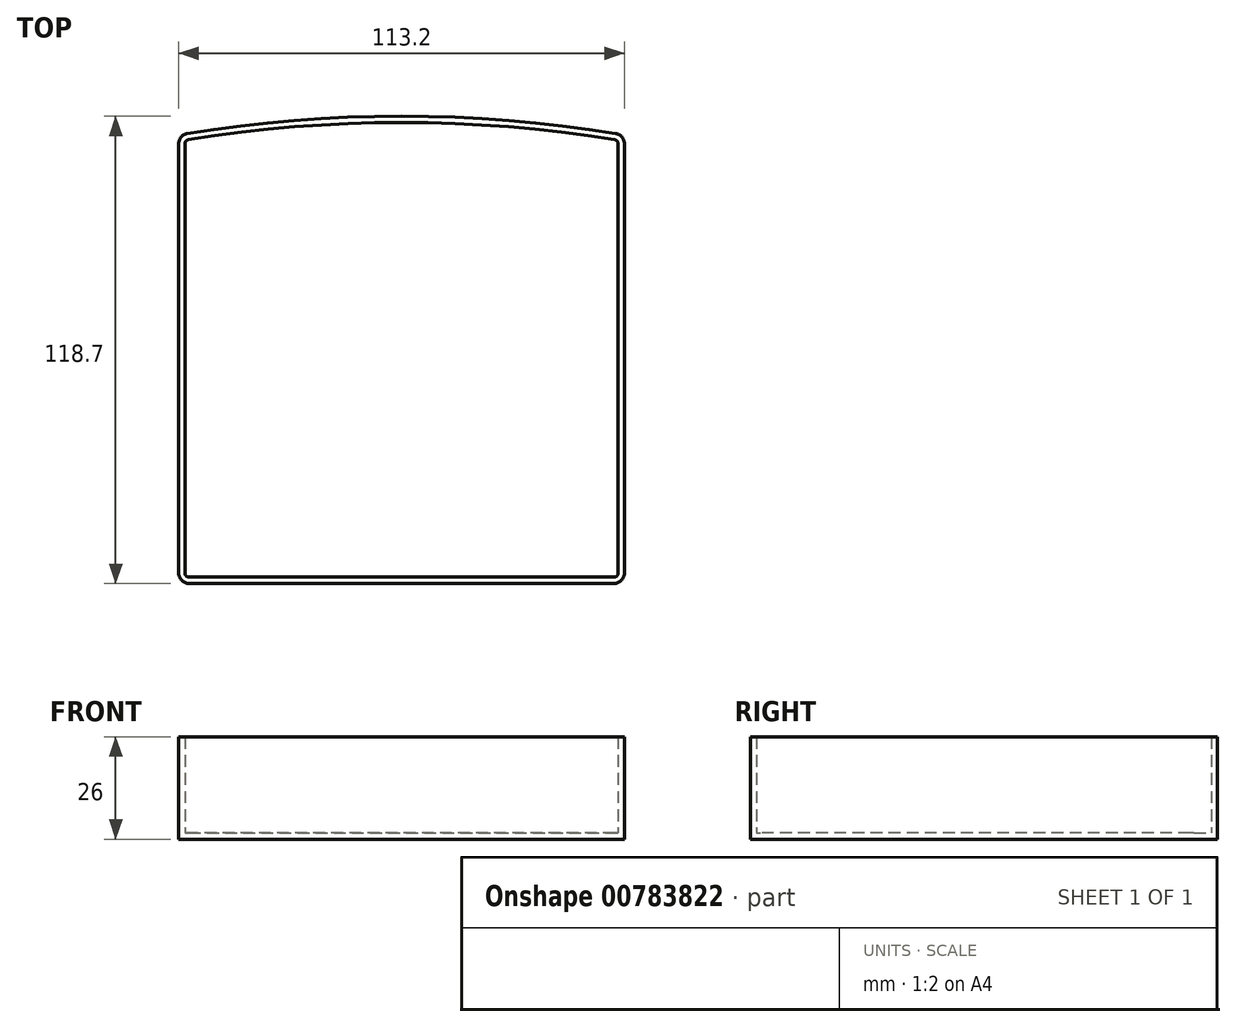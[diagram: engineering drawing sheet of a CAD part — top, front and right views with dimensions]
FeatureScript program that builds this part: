
annotation { "Feature Type Name" : "Feature", "Feature Type Description" : "" }
export const myFeature = defineFeature(function(context is Context, id is Id, definition is map)
    precondition{}
    {
        {
            var Q0;
            Q0=qCreatedBy(makeId("Top.planeOp"),FACE);
            var sketch = newSketch(context, id + "F0", { "sketchPlane" : qUnion([Q0])});
            skLineSegment(sketch, "E0.top", {"start": v(-54, -55.5) * mm, "end": v(54, -55.5) * mm});
            skLineSegment(sketch, "E0.left", {"start": v(-55, 54.65) * mm, "end": v(-55, -54.5) * mm});
            skLineSegment(sketch, "E0.right", {"start": v(55, 54.65) * mm, "end": v(55, -54.5) * mm});
            skLineSegment(sketch, "E1", {"start": v(-55, 0) * mm, "end": v(55, 0) * mm, "construction": true});
            skArc(sketch, "E2", {"start": v(54.16, 55.64) * mm, "mid": v(0, 60) * mm, "end": v(-54.16, 55.64) * mm});
            skPoint(sketch, "E3.visualSharp", {"position": v(-55, -55.5) * mm});
            skArc(sketch, "E3.filletArc", {"start": v(-55, -54.5) * mm, "mid": v(-54.7, -55.2) * mm, "end": v(-54, -55.5) * mm});
            skPoint(sketch, "E4.visualSharp", {"position": v(55, -55.5) * mm});
            skArc(sketch, "E4.filletArc", {"start": v(54, -55.5) * mm, "mid": v(54.7, -55.2) * mm, "end": v(55, -54.5) * mm});
            skPoint(sketch, "E5.visualSharp", {"position": v(55, 55.5) * mm});
            skArc(sketch, "E5.filletArc", {"start": v(55, 54.65) * mm, "mid": v(54.76, 55.3) * mm, "end": v(54.16, 55.64) * mm});
            skPoint(sketch, "E6.visualSharp", {"position": v(-55, 55.5) * mm});
            skArc(sketch, "E6.filletArc", {"start": v(-54.16, 55.64) * mm, "mid": v(-54.76, 55.3) * mm, "end": v(-55, 54.65) * mm});
            skArc(sketch, "E7.0", {"start": v(-54.42, 57.22) * mm, "mid": v(-55.98, 56.34) * mm, "end": v(-56.6, 54.65) * mm});
            skArc(sketch, "E7.1", {"start": v(54.42, 57.22) * mm, "mid": v(0, 61.6) * mm, "end": v(-54.42, 57.22) * mm});
            skLineSegment(sketch, "E7.2", {"start": v(-56.6, 54.65) * mm, "end": v(-56.6, -54.5) * mm});
            skArc(sketch, "E7.3", {"start": v(56.6, 54.65) * mm, "mid": v(55.98, 56.34) * mm, "end": v(54.42, 57.22) * mm});
            skArc(sketch, "E7.4", {"start": v(-56.6, -54.5) * mm, "mid": v(-55.84, -56.34) * mm, "end": v(-54, -57.1) * mm});
            skLineSegment(sketch, "E7.5", {"start": v(-54, -57.1) * mm, "end": v(54, -57.1) * mm});
            skArc(sketch, "E7.6", {"start": v(54, -57.1) * mm, "mid": v(55.84, -56.34) * mm, "end": v(56.6, -54.5) * mm});
            skLineSegment(sketch, "E7.7", {"start": v(56.6, 54.65) * mm, "end": v(56.6, -54.5) * mm});
            skLineSegment(sketch, "E8", {"start": v(0, 60) * mm, "end": v(0, 55.5) * mm, "construction": true});
            skLineSegment(sketch, "E9", {"start": v(0, 55.5) * mm, "end": v(55, 55.5) * mm, "construction": true});
            skLineSegment(sketch, "E10", {"start": v(-55, 55.5) * mm, "end": v(0, 55.5) * mm, "construction": true});
            skSolve(sketch);
        }
        {
            var Q0;
            Q0=makeQuery(id+"F0.imprint","IMPRINT",FACE,{"disambiguationData":[TD([[makeQuery(id+"F0.imprint","IMPRINT",EDGE,{"derivedFrom":sQuery(id+"F0.wireOp",EDGE,"E0.top")}),-1.0]])]});
            extrude(context, id + "F1", {"entities" : qUnion([Q0]), "depth" : 26 * mm, "offsetDistance" : 25 * mm});
        }
        {
            var Q0;
            Q0=makeQuery(id+"F0.imprint","IMPRINT",FACE,{"disambiguationData":[TD([[makeQuery(id+"F0.imprint","IMPRINT",EDGE,{"derivedFrom":sQuery(id+"F0.wireOp",EDGE,"E0.top")}),1.0]])]});
            extrude(context, id + "F2", {"entities" : qUnion([Q0]), "operationType" : NewBodyOperationType.ADD, "depth" : 1.6 * mm, "offsetDistance" : 25 * mm});
        }
    });
